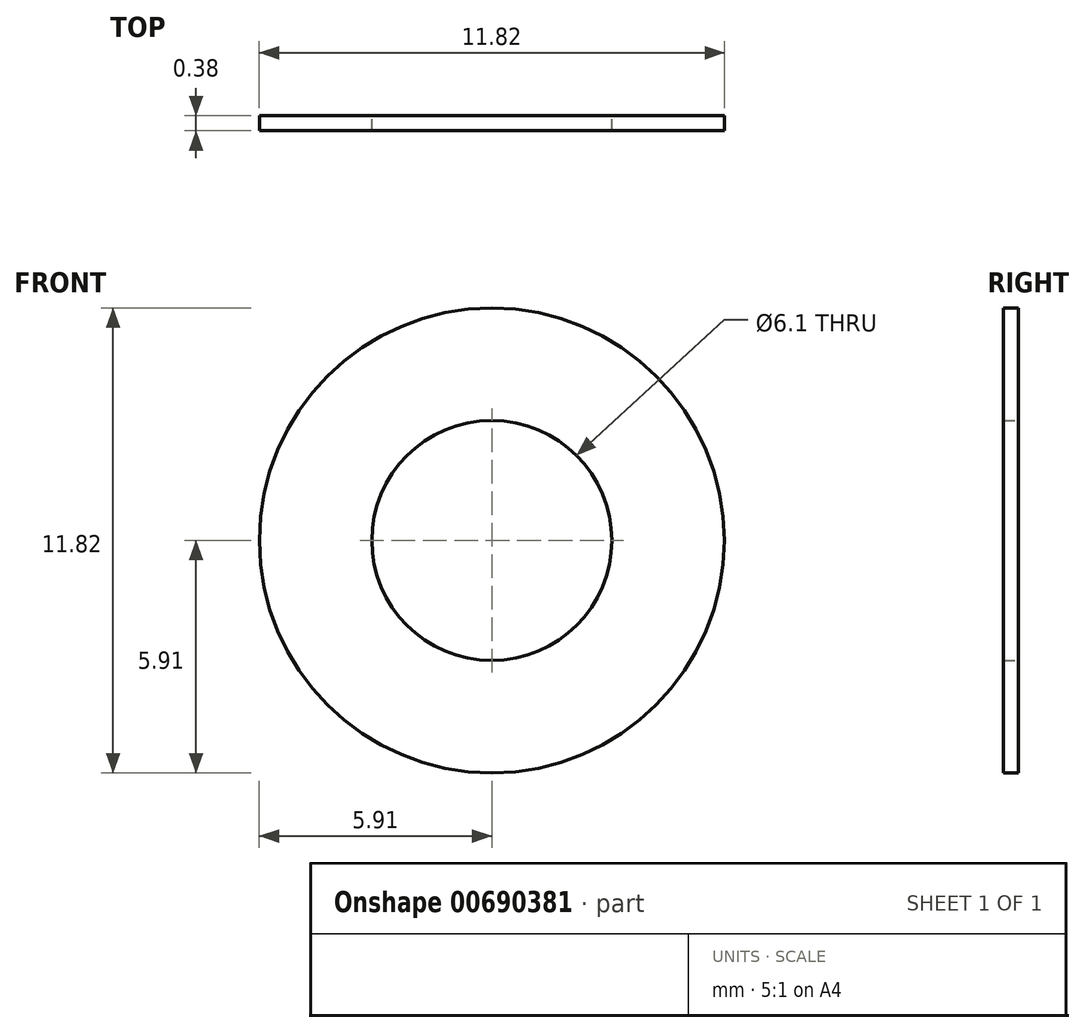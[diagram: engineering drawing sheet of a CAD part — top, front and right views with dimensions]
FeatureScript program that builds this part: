
annotation { "Feature Type Name" : "Feature", "Feature Type Description" : "" }
export const myFeature = defineFeature(function(context is Context, id is Id, definition is map)
    precondition{}
    {
        {
            var Q0;
            Q0=qCreatedBy(makeId("Front.planeOp"),FACE);
            var sketch = newSketch(context, id + "F0", { "sketchPlane" : qUnion([Q0])});
            skCircle(sketch, "E0", {"center": v(0, 0) * mm, "radius": 5.9 * mm});
            skCircle(sketch, "E1", {"center": v(0, 0) * mm, "radius": 3.05 * mm});
            skSolve(sketch);
        }
        {
            var Q0;
            Q0 = qSketchRegion(id + "F0", true);
            extrude(context, id + "F1", {"entities" : qUnion([Q0]), "depth" : 0.38 * mm, "offsetDistance" : 25.4 * mm});
        }
    });
